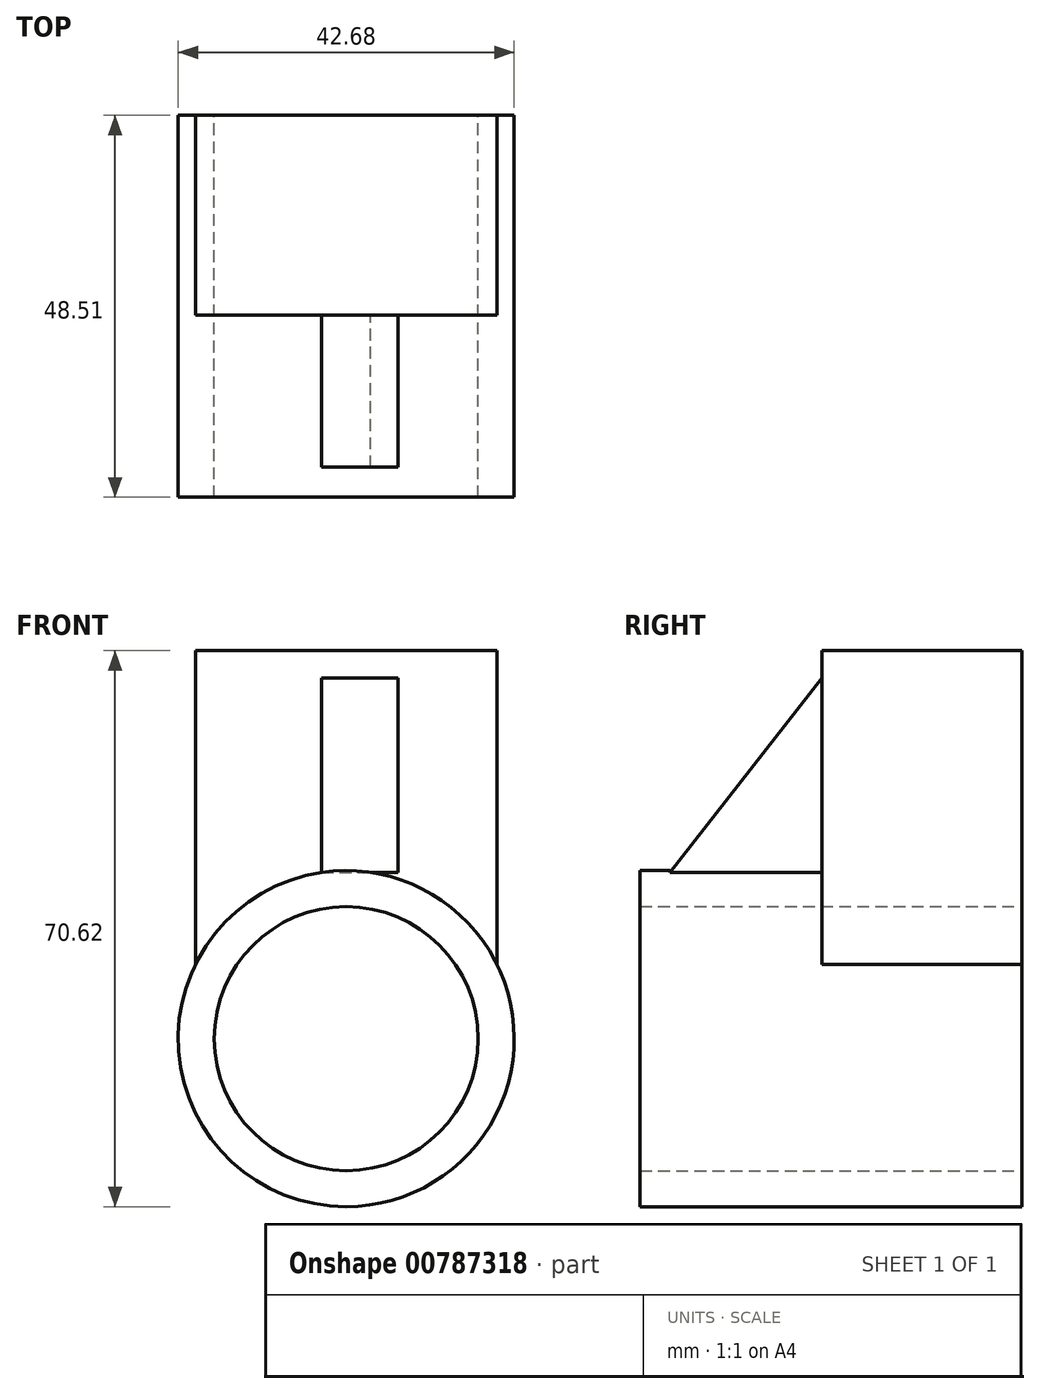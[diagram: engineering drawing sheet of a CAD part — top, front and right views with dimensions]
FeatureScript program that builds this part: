
annotation { "Feature Type Name" : "Feature", "Feature Type Description" : "" }
export const myFeature = defineFeature(function(context is Context, id is Id, definition is map)
    precondition{}
    {
        {
            var Q0;
            Q0=qCreatedBy(makeId("Front.planeOp"),FACE);
            var sketch = newSketch(context, id + "F0", { "sketchPlane" : qUnion([Q0])});
            skCircle(sketch, "E0", {"center": v(0, 0) * mm, "radius": 21.34 * mm});
            skCircle(sketch, "E1", {"center": v(0, 0) * mm, "radius": 16.77 * mm});
            skLineSegment(sketch, "E2.bottom", {"start": v(-19.14, 9.45) * mm, "end": v(19.16, 9.45) * mm});
            skLineSegment(sketch, "E2.top", {"start": v(-19.14, 49.28) * mm, "end": v(19.16, 49.28) * mm});
            skLineSegment(sketch, "E2.left", {"start": v(-19.14, 9.45) * mm, "end": v(-19.14, 49.28) * mm});
            skLineSegment(sketch, "E2.right", {"start": v(19.16, 9.45) * mm, "end": v(19.16, 49.28) * mm});
            skSolve(sketch);
        }
        {
            var Q0;
            Q0=makeQuery(id+"F0.imprint","IMPRINT",FACE,{"disambiguationData":[TD([[makeQuery(id+"F0.imprint","IMPRINT",EDGE,{"derivedFrom":sQuery(id+"F0.wireOp",EDGE,"E2.top")}),-1.0]])]});
            extrude(context, id + "F1", {"entities" : qUnion([Q0]), "depth" : 25.4 * mm, "offsetDistance" : 25.4 * mm});
        }
        {
            var Q0;
            {var subQ0=sQuery(id+"F0.wireOp",EDGE,"E2.bottom");var subQ4=sQuery(id+"F0.wireOp",EDGE,"E1");var subQ6=makeQuery(id+"F0.imprint","INTERSECT",VERTEX,{"disambiguationData":[OD(0.0)],"derivedFrom":[subQ4,subQ0]});Q0=makeQuery(id+"F0.imprint","IMPRINT",FACE,{"disambiguationData":[TD([[makeQuery(id+"F0.imprint","IMPRINT",EDGE,{"disambiguationData":[TD([[subQ6,-1.0]])],"derivedFrom":subQ4}),-1.0]])]});}
            var Q1;
            {var subQ0=sQuery(id+"F0.wireOp",EDGE,"E2.bottom");var subQ4=sQuery(id+"F0.wireOp",EDGE,"E1");var subQ5=makeQuery(id+"F0.imprint","INTERSECT",VERTEX,{"disambiguationData":[OD(0.0)],"derivedFrom":[subQ4,subQ0]});Q1=makeQuery(id+"F0.imprint","IMPRINT",FACE,{"disambiguationData":[TD([[makeQuery(id+"F0.imprint","IMPRINT",EDGE,{"disambiguationData":[TD([[subQ5,1.0]])],"derivedFrom":subQ4}),-1.0]])]});}
            extrude(context, id + "F2", {"entities" : qUnion([Q0, Q1]), "operationType" : NewBodyOperationType.ADD, "depth" : 48.5 * mm, "offsetDistance" : 25.4 * mm});
        }
        {
            var Q0;
            Q0=makeQuery(id+"F1.opExtrude","CAP_FACE",FACE,{"disambiguationData":[OSD([sQuery(id+"F0.wireOp",EDGE,"E0"),sQuery(id+"F0.wireOp",EDGE,"E2.bottom"),sQuery(id+"F0.wireOp",EDGE,"E2.top"),sQuery(id+"F0.wireOp",EDGE,"E2.left"),sQuery(id+"F0.wireOp",EDGE,"E2.right")])],"isStart":false});
            var sketch = newSketch(context, id + "F3", { "sketchPlane" : qUnion([Q0])});
            skLineSegment(sketch, "E3.bottom", {"start": v(-3.12, 21.11) * mm, "end": v(6.6, 21.11) * mm});
            skLineSegment(sketch, "E3.top", {"start": v(-3.12, 45.85) * mm, "end": v(6.6, 45.85) * mm});
            skLineSegment(sketch, "E3.left", {"start": v(-3.12, 21.11) * mm, "end": v(-3.12, 45.85) * mm});
            skLineSegment(sketch, "E3.right", {"start": v(6.6, 21.11) * mm, "end": v(6.6, 45.85) * mm});
            skSolve(sketch);
        }
        {
            var Q0;
            Q0=makeQuery(id+"F3.imprint","IMPRINT",FACE,{"disambiguationData":[TD([[makeQuery(id+"F3.imprint","IMPRINT",EDGE,{"derivedFrom":sQuery(id+"F3.wireOp",EDGE,"E3.top")}),-1.0]])]});
            extrude(context, id + "F4", {"entities" : qUnion([Q0]), "operationType" : NewBodyOperationType.ADD, "depth" : 19.3 * mm, "offsetDistance" : 25.4 * mm});
        }
        {
            var Q0;
            Q0=makeQuery(id+"F4.opExtrude","SWEPT_FACE",FACE,{"disambiguationData":[OSD([sQuery(id+"F3.wireOp",EDGE,"E3.right")])]});
            var sketch = newSketch(context, id + "F5", { "sketchPlane" : qUnion([Q0])});
            skLineSegment(sketch, "E4", {"start": v(-44.7, 21.11) * mm, "end": v(-25.4, 45.85) * mm});
            skSolve(sketch);
        }
        {
            var Q0;
            Q0=makeQuery(id+"F5.imprint","IMPRINT",FACE,{"disambiguationData":[TD([[makeQuery(id+"F5.imprint","IMPRINT",EDGE,{"derivedFrom":sQuery(id+"F5.wireOp",EDGE,"E4")}),1.0]])]});
            extrude(context, id + "F6", {"entities" : qUnion([Q0]), "operationType" : NewBodyOperationType.REMOVE, "oppositeDirection" : true, "depth" : 25.4 * mm, "offsetDistance" : 25.4 * mm});
        }
    });
